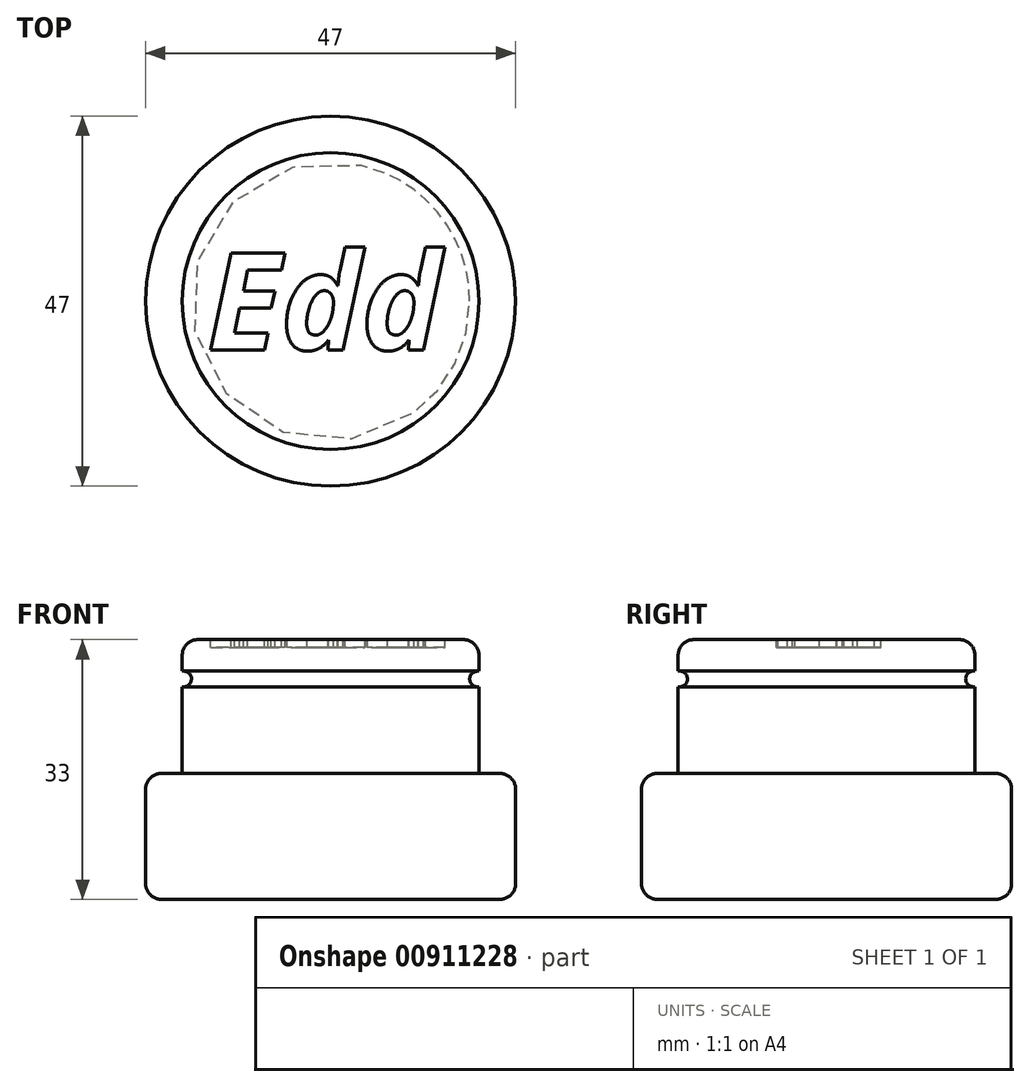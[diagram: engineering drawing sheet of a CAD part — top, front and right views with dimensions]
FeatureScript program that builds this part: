
annotation { "Feature Type Name" : "Feature", "Feature Type Description" : "" }
export const myFeature = defineFeature(function(context is Context, id is Id, definition is map)
    precondition{}
    {
        {
            var Q0;
            Q0=qCreatedBy(makeId("Top.planeOp"),FACE);
            var sketch = newSketch(context, id + "F0", { "sketchPlane" : qUnion([Q0])});
            skCircle(sketch, "E0", {"center": v(0, 0) * mm, "radius": 23.5 * mm});
            skCircle(sketch, "E1", {"center": v(0, 0) * mm, "radius": 18.85 * mm});
            skSolve(sketch);
        }
        {
            var Q0;
            Q0=makeQuery(id+"F0.imprint","IMPRINT",FACE,{"disambiguationData":[TD([[makeQuery(id+"F0.imprint","IMPRINT",EDGE,{"derivedFrom":sQuery(id+"F0.wireOp",EDGE,"E0")}),1.0]])]});
            extrude(context, id + "F1", {"entities" : qUnion([Q0]), "depth" : 16 * mm, "offsetDistance" : 25 * mm});
        }
        {
            var Q0;
            Q0=makeQuery(id+"F0.imprint","IMPRINT",FACE,{"disambiguationData":[TD([[makeQuery(id+"F0.imprint","IMPRINT",EDGE,{"derivedFrom":sQuery(id+"F0.wireOp",EDGE,"E1")}),1.0]])]});
            extrude(context, id + "F2", {"entities" : qUnion([Q0]), "operationType" : NewBodyOperationType.ADD, "depth" : (17 + 16) * mm, "offsetDistance" : 25 * mm});
        }
        {
            var Q0;
            Q0=makeQuery(id+"F2.opExtrude","CAP_EDGE",EDGE,{"disambiguationData":[OSD([sQuery(id+"F0.wireOp",EDGE,"E1")])],"isStart":false});
            var Q1;
            Q1=makeQuery(id+"F1.opExtrude","CAP_EDGE",EDGE,{"disambiguationData":[OSD([sQuery(id+"F0.wireOp",EDGE,"E0")])],"isStart":false});
            var Q2;
            Q2=makeQuery(id+"F1.opExtrude","CAP_EDGE",EDGE,{"disambiguationData":[OSD([sQuery(id+"F0.wireOp",EDGE,"E0")])],"isStart":true});
            fillet(context, id + "F3", {"entities" : qUnion([Q0, Q1, Q2]), "radius" : 2 * mm, "tangentPropagation" : true, "allowEdgeOverflow" : false});
        }
        {
            var Q0;
            Q0=qCreatedBy(makeId("Front.planeOp"),FACE);
            var sketch = newSketch(context, id + "F4", { "sketchPlane" : qUnion([Q0])});
            skLineSegment(sketch, "E2", {"start": v(0, 0) * mm, "end": v(0, 37.79) * mm, "construction": true});
            skLineSegment(sketch, "E3", {"start": v(0, 16) * mm, "end": v(30.35, 16) * mm, "construction": true});
            skLineSegment(sketch, "E4", {"start": v(0, 33) * mm, "end": v(28.16, 33) * mm, "construction": true});
            skCircle(sketch, "E5", {"center": v(18.67, 28) * mm, "radius": 1 * mm});
            skLineSegment(sketch, "E6", {"start": v(18.65, 29) * mm, "end": v(18.95, 29) * mm});
            skLineSegment(sketch, "E7", {"start": v(18.95, 29) * mm, "end": v(18.95, 28.96) * mm});
            skLineSegment(sketch, "E8", {"start": v(18.67, 27) * mm, "end": v(19.13, 27) * mm});
            skLineSegment(sketch, "E9", {"start": v(19.13, 27) * mm, "end": v(19.13, 27.11) * mm});
            skSolve(sketch);
        }
        {
            var Q0;
            Q0 = qSketchRegion(id + "F4", true);
            var Q1;
            Q1=sQuery(id+"F4.wireOp",EDGE,"E2");
            revolve(context, id + "F5", {"operationType" : NewBodyOperationType.REMOVE, "surfaceOperationType" : NewSurfaceOperationType.NEW, "entities" : qUnion([Q0]), "axis" : qUnion([Q1]), "revolveType" : RevolveType.FULL, "oppositeDirection" : true});
        }
        {
            var Q0;
            Q0=makeQuery(id+"F2.opExtrude","CAP_FACE",FACE,{"disambiguationData":[OSD([sQuery(id+"F0.wireOp",EDGE,"E1")])],"isStart":false});
            var sketch = newSketch(context, id + "F6", { "sketchPlane" : qUnion([Q0])});
            skText(sketch, "E10", { "text": "Edd", "fontName": "OpenSans-BoldItalic.ttf"});
            const initialGuessF6  = {"E10": [-0.01567, -0.00619, 1, 0, 0.01238]};
            skSetInitialGuess(sketch, initialGuessF6);
            skSolve(sketch);
        }
        {
            var Q0;
            Q0=makeQuery(id+"F6.imprint","IMPRINT",FACE,{"disambiguationData":[TD([[makeQuery(id+"F6.imprint","IMPRINT",EDGE,{"derivedFrom":sQuery(id+"F6.wireOp",EDGE,"E10.sketch_text.stroke-0")}),-1.0]])]});
            var Q1;
            Q1=makeQuery(id+"F6.imprint","IMPRINT",FACE,{"disambiguationData":[TD([[makeQuery(id+"F6.imprint","IMPRINT",EDGE,{"derivedFrom":sQuery(id+"F6.wireOp",EDGE,"E10.sketch_text.stroke-12")}),-1.0]])]});
            var Q2;
            Q2=makeQuery(id+"F6.imprint","IMPRINT",FACE,{"disambiguationData":[TD([[makeQuery(id+"F6.imprint","IMPRINT",EDGE,{"derivedFrom":sQuery(id+"F6.wireOp",EDGE,"E10.sketch_text.stroke-39")}),-1.0]])]});
            extrude(context, id + "F7", {"entities" : qUnion([Q0, Q1, Q2]), "operationType" : NewBodyOperationType.REMOVE, "oppositeDirection" : true, "depth" : 1 * mm, "offsetDistance" : 25 * mm});
        }
    });
